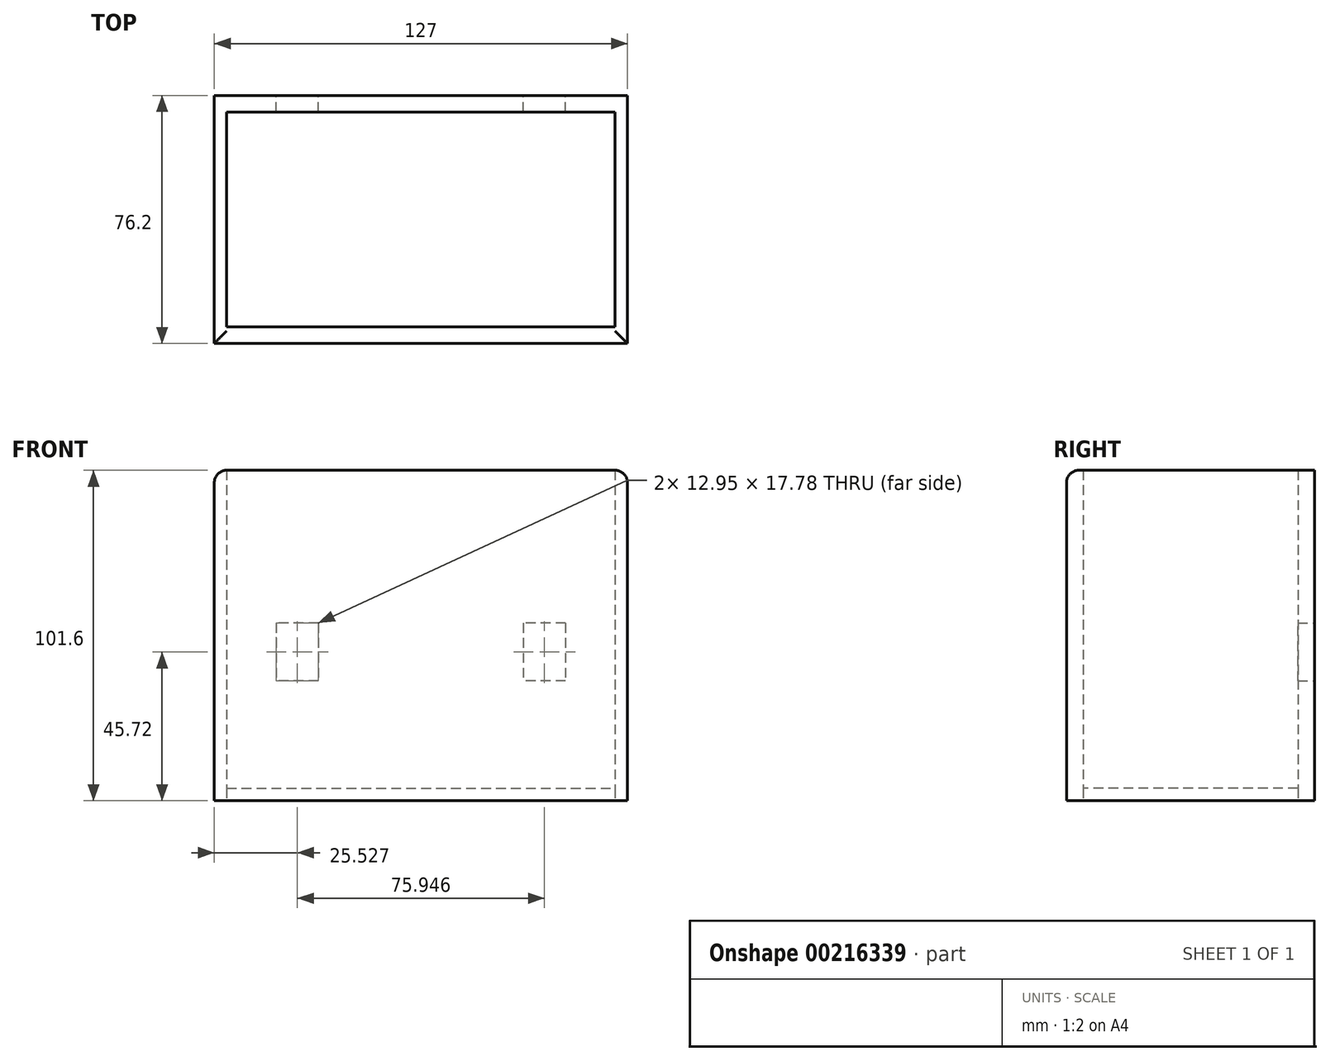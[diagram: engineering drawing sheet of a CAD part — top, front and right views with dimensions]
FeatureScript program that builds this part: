
annotation { "Feature Type Name" : "Feature", "Feature Type Description" : "" }
export const myFeature = defineFeature(function(context is Context, id is Id, definition is map)
    precondition{}
    {
        {
            var Q0;
            Q0=qCreatedBy(makeId("Top.planeOp"),FACE);
            var sketch = newSketch(context, id + "F0", { "sketchPlane" : qUnion([Q0])});
            skLineSegment(sketch, "E0.bottom", {"start": v(-63.5, 38.1) * mm, "end": v(63.5, 38.1) * mm});
            skLineSegment(sketch, "E0.top", {"start": v(-63.5, -38.1) * mm, "end": v(63.5, -38.1) * mm});
            skLineSegment(sketch, "E0.left", {"start": v(-63.5, 38.1) * mm, "end": v(-63.5, -38.1) * mm});
            skLineSegment(sketch, "E0.right", {"start": v(63.5, 38.1) * mm, "end": v(63.5, -38.1) * mm});
            skPoint(sketch, "E0.middle", {"position": v(0, 0) * mm});
            skLineSegment(sketch, "E1.bottom", {"start": v(-59.7, 33.02) * mm, "end": v(59.7, 33.02) * mm});
            skLineSegment(sketch, "E1.top", {"start": v(-59.7, -33.02) * mm, "end": v(59.7, -33.02) * mm});
            skLineSegment(sketch, "E1.left", {"start": v(-59.69, 33.02) * mm, "end": v(-59.7, -33.02) * mm});
            skLineSegment(sketch, "E1.right", {"start": v(59.7, 33.02) * mm, "end": v(59.69, -33.02) * mm});
            skSolve(sketch);
        }
        {
            var Q0;
            Q0=makeQuery(id+"F0.imprint","IMPRINT",FACE,{"disambiguationData":[TD([[makeQuery(id+"F0.imprint","IMPRINT",EDGE,{"derivedFrom":sQuery(id+"F0.wireOp",EDGE,"E0.bottom")}),-1.0]])]});
            extrude(context, id + "F1", {"entities" : qUnion([Q0]), "depth" : 101.6 * mm});
        }
        {
            var Q0;
            Q0=makeQuery(id+"F1.opExtrude","SWEPT_FACE",FACE,{"disambiguationData":[OSD([sQuery(id+"F0.wireOp",EDGE,"E0.bottom")])]});
            var sketch = newSketch(context, id + "F2", { "sketchPlane" : qUnion([Q0])});
            skLineSegment(sketch, "E2.bottom", {"start": v(-44.45, 54.61) * mm, "end": v(-31.5, 54.61) * mm});
            skLineSegment(sketch, "E2.top", {"start": v(-44.45, 36.83) * mm, "end": v(-31.5, 36.83) * mm});
            skLineSegment(sketch, "E2.left", {"start": v(-44.45, 54.61) * mm, "end": v(-44.45, 36.83) * mm});
            skLineSegment(sketch, "E2.right", {"start": v(-31.5, 54.61) * mm, "end": v(-31.5, 36.83) * mm});
            skLineSegment(sketch, "E3.bottom", {"start": v(31.5, 54.61) * mm, "end": v(44.45, 54.61) * mm});
            skLineSegment(sketch, "E3.top", {"start": v(31.5, 36.83) * mm, "end": v(44.45, 36.83) * mm});
            skLineSegment(sketch, "E3.left", {"start": v(31.5, 54.61) * mm, "end": v(31.5, 36.83) * mm});
            skLineSegment(sketch, "E3.right", {"start": v(44.45, 54.61) * mm, "end": v(44.45, 36.83) * mm});
            skSolve(sketch);
        }
        {
            var Q0;
            Q0=makeQuery(id+"F2.imprint","IMPRINT",FACE,{"disambiguationData":[TD([[makeQuery(id+"F2.imprint","IMPRINT",EDGE,{"derivedFrom":sQuery(id+"F2.wireOp",EDGE,"E2.bottom")}),-1.0]])]});
            var Q1;
            Q1=makeQuery(id+"F2.imprint","IMPRINT",FACE,{"disambiguationData":[TD([[makeQuery(id+"F2.imprint","IMPRINT",EDGE,{"derivedFrom":sQuery(id+"F2.wireOp",EDGE,"E3.bottom")}),-1.0]])]});
            extrude(context, id + "F3", {"entities" : qUnion([Q0, Q1]), "operationType" : NewBodyOperationType.REMOVE, "endBound" : BoundingType.UP_TO_NEXT, "oppositeDirection" : true, "depth" : 25.4 * mm});
        }
        {
            var Q0;
            Q0=makeQuery(id+"F1.opExtrude","CAP_FACE",FACE,{"disambiguationData":[OSD([sQuery(id+"F0.wireOp",EDGE,"E0.bottom"),sQuery(id+"F0.wireOp",EDGE,"E0.top"),sQuery(id+"F0.wireOp",EDGE,"E0.left"),sQuery(id+"F0.wireOp",EDGE,"E0.right"),sQuery(id+"F0.wireOp",EDGE,"E1.bottom"),sQuery(id+"F0.wireOp",EDGE,"E1.top"),sQuery(id+"F0.wireOp",EDGE,"E1.left"),sQuery(id+"F0.wireOp",EDGE,"E1.right")])],"isStart":true});
            var sketch = newSketch(context, id + "F4", { "sketchPlane" : qUnion([Q0])});
            skLineSegment(sketch, "E4.bottom", {"start": v(59.7, -33.02) * mm, "end": v(-59.7, -33.02) * mm});
            skLineSegment(sketch, "E4.top", {"start": v(59.7, 33.02) * mm, "end": v(-59.7, 33.02) * mm});
            skLineSegment(sketch, "E4.left", {"start": v(59.7, -33.02) * mm, "end": v(59.7, 33.02) * mm});
            skLineSegment(sketch, "E4.right", {"start": v(-59.7, -33.02) * mm, "end": v(-59.7, 33.02) * mm});
            skSolve(sketch);
        }
        {
            var Q0;
            Q0=makeQuery(id+"F4.imprint","IMPRINT",FACE,{"disambiguationData":[TD([[makeQuery(id+"F4.imprint","IMPRINT",EDGE,{"derivedFrom":sQuery(id+"F4.wireOp",EDGE,"E4.bottom")}),1.0]])]});
            extrude(context, id + "F5", {"entities" : qUnion([Q0]), "oppositeDirection" : true, "depth" : 3.8 * mm});
        }
        {
            var Q0;
            Q0=makeQuery(id+"F1.opExtrude","CAP_EDGE",EDGE,{"disambiguationData":[OSD([sQuery(id+"F0.wireOp",EDGE,"E0.right")])],"isStart":false});
            var Q1;
            Q1=makeQuery(id+"F1.opExtrude","CAP_EDGE",EDGE,{"disambiguationData":[OSD([sQuery(id+"F0.wireOp",EDGE,"E0.top")])],"isStart":false});
            var Q2;
            Q2=makeQuery(id+"F1.opExtrude","CAP_EDGE",EDGE,{"disambiguationData":[OSD([sQuery(id+"F0.wireOp",EDGE,"E0.left")])],"isStart":false});
            fillet(context, id + "F6", {"entities" : qUnion([Q0, Q1, Q2]), "radius" : 3.8 * mm, "tangentPropagation" : true, "allowEdgeOverflow" : false});
        }
    });
